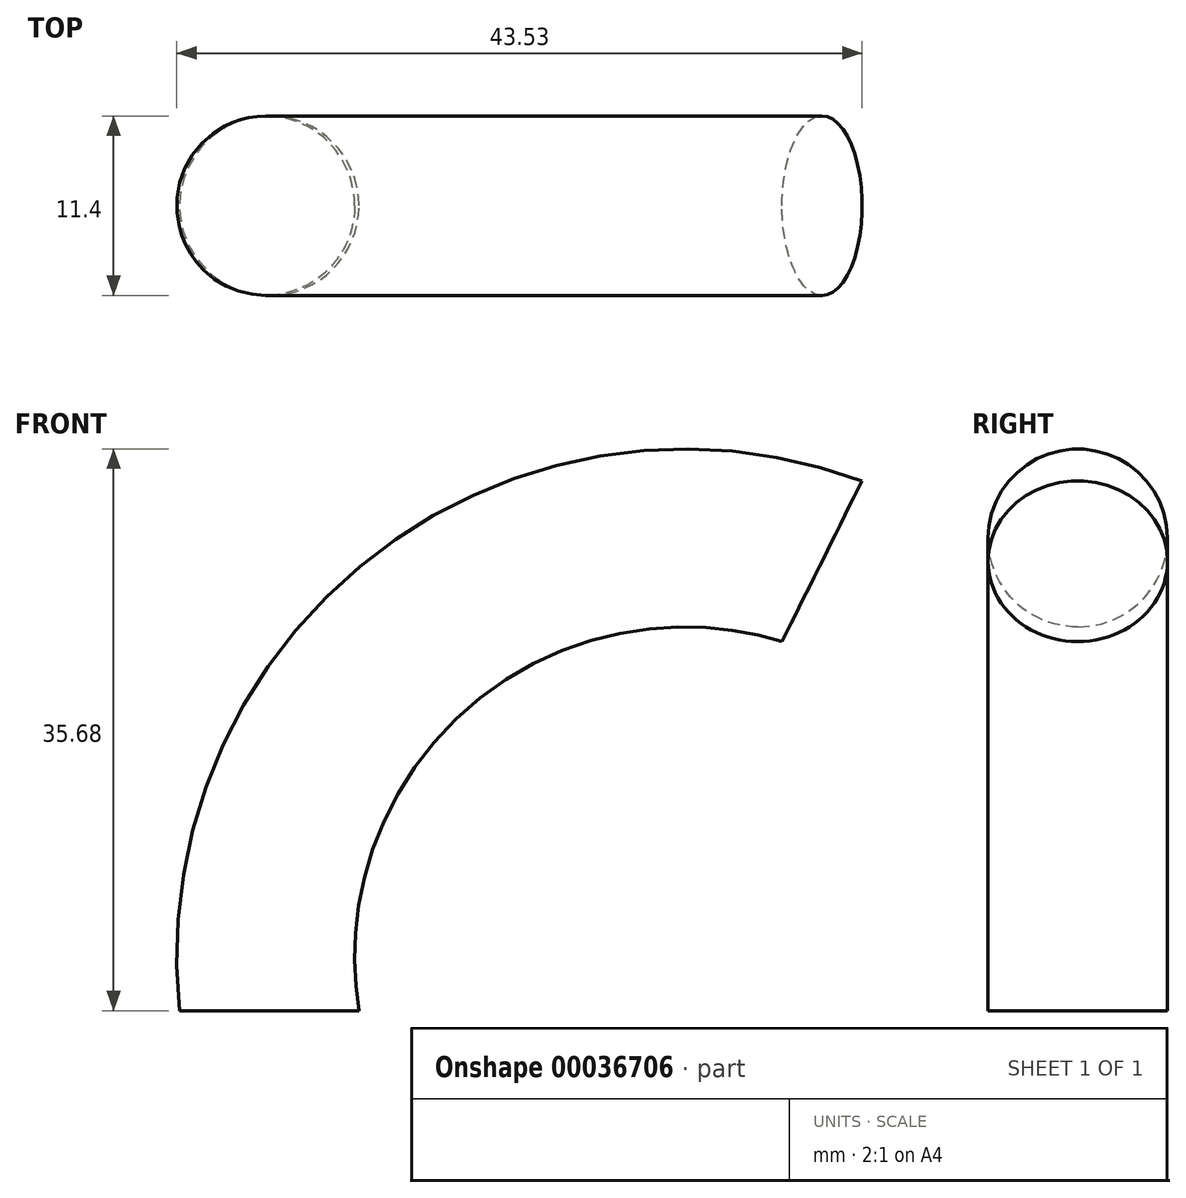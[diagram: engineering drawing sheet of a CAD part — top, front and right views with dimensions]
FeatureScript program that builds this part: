
annotation { "Feature Type Name" : "Feature", "Feature Type Description" : "" }
export const myFeature = defineFeature(function(context is Context, id is Id, definition is map)
    precondition{}
    {
        {
            var Q0;
            Q0=qCreatedBy(makeId("Top.planeOp"),FACE);
            var sketch = newSketch(context, id + "F0", { "sketchPlane" : qUnion([Q0])});
            skCircle(sketch, "E0", {"center": v(0, 0) * mm, "radius": 5.7 * mm});
            skSolve(sketch);
        }
        {
            var Q0;
            Q0=qCreatedBy(makeId("Front.planeOp"),FACE);
            var sketch = newSketch(context, id + "F1", { "sketchPlane" : qUnion([Q0])});
            skArc(sketch, "E1", {"start": v(35.1, 28.55) * mm, "mid": v(9.6, 24.05) * mm, "end": v(0, 0) * mm});
            skSolve(sketch);
        }
        {
            var Q0;
            Q0=makeQuery(id+"F0.imprint","IMPRINT",FACE,{"disambiguationData":[TD([[makeQuery(id+"F0.imprint","IMPRINT",EDGE,{"derivedFrom":sQuery(id+"F0.wireOp",EDGE,"E0")}),1.0]])]});
            var Q1;
            Q1=sQuery(id+"F1.wireOp",EDGE,"E1");
            sweep(context, id + "F2", {"profiles" : qUnion([Q0]), "path" : qUnion([Q1])});
        }
    });
